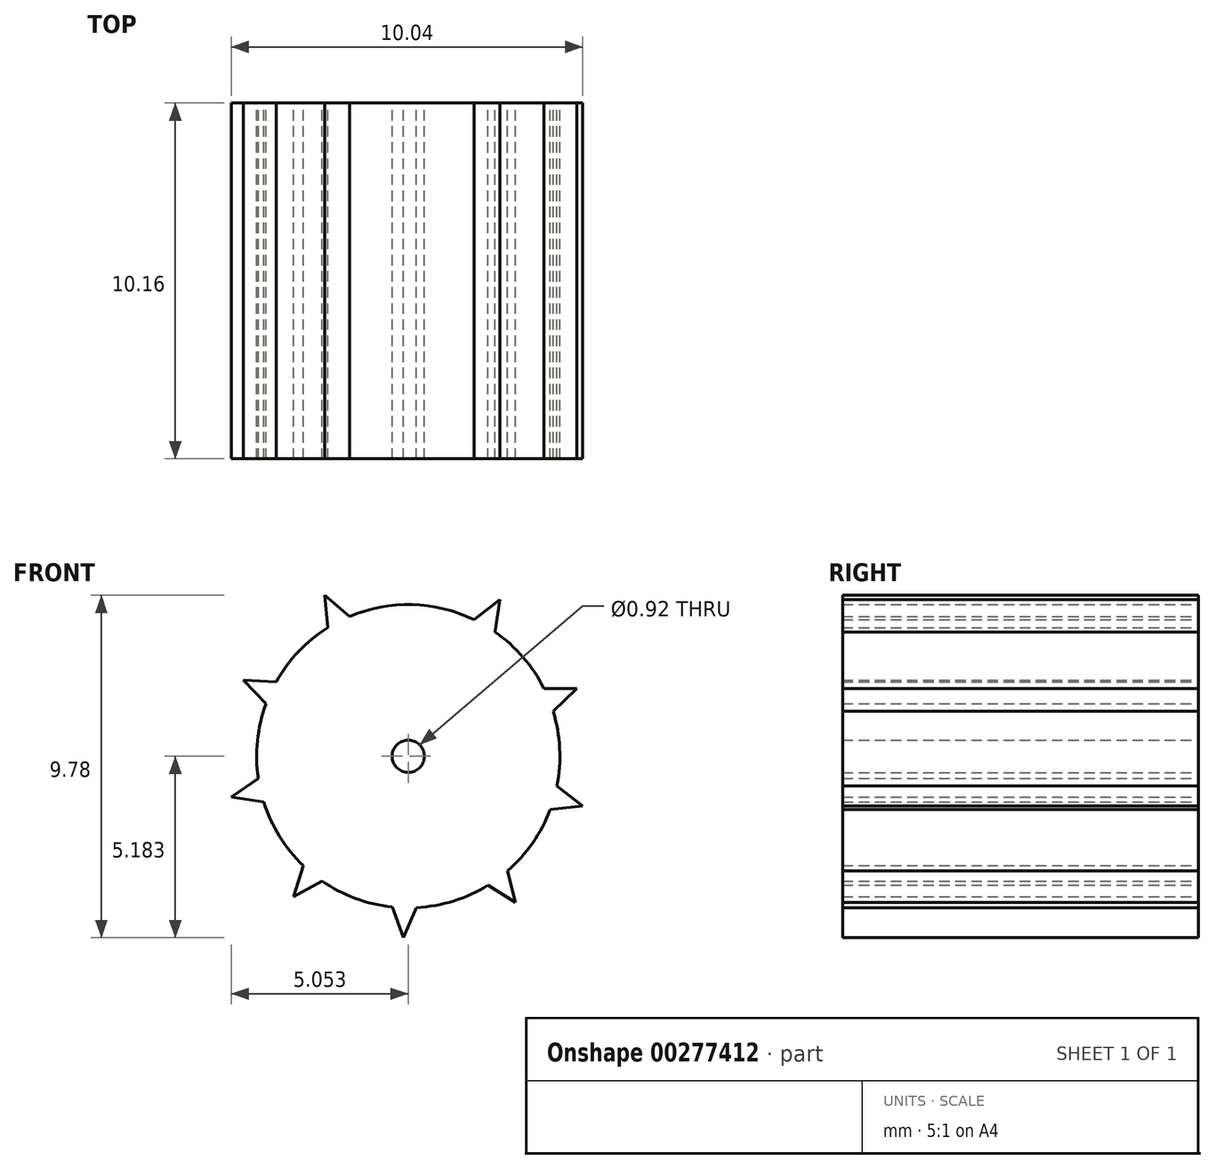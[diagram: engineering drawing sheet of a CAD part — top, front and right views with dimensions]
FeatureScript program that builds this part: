
annotation { "Feature Type Name" : "Feature", "Feature Type Description" : "" }
export const myFeature = defineFeature(function(context is Context, id is Id, definition is map)
    precondition{}
    {
        {
            var Q0;
            Q0=qCreatedBy(makeId("Front.planeOp"),FACE);
            var sketch = newSketch(context, id + "F0", { "sketchPlane" : qUnion([Q0])});
            skCircle(sketch, "E0", {"center": v(-46.79, 23.93) * mm, "radius": 4.33 * mm});
            skLineSegment(sketch, "E1", {"start": v(-44.9, 27.83) * mm, "end": v(-44.17, 28.4) * mm});
            skLineSegment(sketch, "E2", {"start": v(-44.3, 27.48) * mm, "end": v(-44.17, 28.4) * mm});
            skLineSegment(sketch, "E3.1.0", {"start": v(-42.91, 25.86) * mm, "end": v(-41.98, 25.86) * mm});
            skLineSegment(sketch, "E3.1.1", {"start": v(-42.65, 25.22) * mm, "end": v(-41.98, 25.86) * mm});
            skLineSegment(sketch, "E3.2.0", {"start": v(-42.54, 23.08) * mm, "end": v(-41.8, 22.51) * mm});
            skLineSegment(sketch, "E3.2.1", {"start": v(-42.73, 22.42) * mm, "end": v(-41.8, 22.51) * mm});
            skLineSegment(sketch, "E3.3.0", {"start": v(-43.95, 20.66) * mm, "end": v(-43.72, 19.76) * mm});
            skLineSegment(sketch, "E3.3.1", {"start": v(-44.51, 20.25) * mm, "end": v(-43.72, 19.76) * mm});
            skLineSegment(sketch, "E3.4.0", {"start": v(-46.55, 19.6) * mm, "end": v(-46.92, 18.75) * mm});
            skLineSegment(sketch, "E3.4.1", {"start": v(-47.24, 19.63) * mm, "end": v(-46.92, 18.75) * mm});
            skLineSegment(sketch, "E3.5.0", {"start": v(-49.25, 20.37) * mm, "end": v(-50.07, 19.92) * mm});
            skLineSegment(sketch, "E3.5.1", {"start": v(-49.79, 20.81) * mm, "end": v(-50.07, 19.92) * mm});
            skLineSegment(sketch, "E3.6.0", {"start": v(-50.92, 22.63) * mm, "end": v(-51.84, 22.77) * mm});
            skLineSegment(sketch, "E3.6.1", {"start": v(-51.07, 23.3) * mm, "end": v(-51.84, 22.77) * mm});
            skLineSegment(sketch, "E3.7.0", {"start": v(-50.85, 25.43) * mm, "end": v(-51.5, 26.1) * mm});
            skLineSegment(sketch, "E3.7.1", {"start": v(-50.56, 26.06) * mm, "end": v(-51.5, 26.1) * mm});
            skLineSegment(sketch, "E3.8.0", {"start": v(-49.08, 27.6) * mm, "end": v(-49.17, 28.53) * mm});
            skLineSegment(sketch, "E3.8.1", {"start": v(-48.47, 27.93) * mm, "end": v(-49.17, 28.53) * mm});
            skLineSegment(sketch, "E3.anchor1", {"start": v(-46.79, 23.93) * mm, "end": v(-44.9, 27.83) * mm, "construction": true});
            skLineSegment(sketch, "E3.anchor2", {"start": v(-46.79, 23.93) * mm, "end": v(-46.35, 28.24) * mm, "construction": true});
            skCircle(sketch, "E4", {"center": v(-46.79, 23.93) * mm, "radius": 0.46 * mm});
            skSolve(sketch);
        }
        {
            var Q0;
            Q0=qSketchRegion(id+"F0",true);
            extrude(context, id + "F1", {"entities" : qUnion([Q0]), "depth" : 5.08 * mm, "hasSecondDirection" : true, "secondDirectionOppositeDirection" : true, "secondDirectionDepth" : 5.08 * mm});
        }
    });
